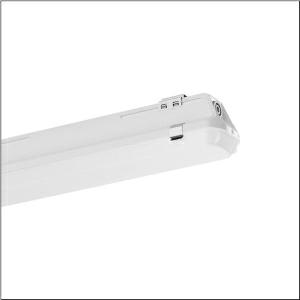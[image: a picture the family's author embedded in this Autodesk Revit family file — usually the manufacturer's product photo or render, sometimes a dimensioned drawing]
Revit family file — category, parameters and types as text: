
# Revit family: monsun_r__21_51fb107p420b_fb8a
name_source: partatom
category: Lighting Fixtures
units: mm (PartAtom-declared; Revit-internal decimal feet)

## family parameters
Cut with Voids When Loaded = No
Host = Face
Light Source = No
Part Type = Normal
Room Calculation Point = No
Round Connector Dimension = Use Diameter
Shared = No

## types (1)
- Monsun® 21 (1 x LED, 2580 lm, 17.5 W, 4000K)
    Apparent Load = 18 VA
    CIE Flux Codes = 47 77 93 94 100
    Color Rendering = 80
    Color Temperature = 4000K
    Default Elevation = 1800 mm
    Description = Monsun® 21, damp-proof luminaire, chain hanger, primary optical cover: enclosure, of PMMA, light emission: direct distribution, primary light characteristic: symmetric, installation type: suspended mounting, surface-mounted, horizontal mounting, vertical mounting, LED, rated luminous flux: 2.580lm, luminous efficacy: 147lm/W, light colour: 840, colour temperature: 4000K, control gear: ECG, with terminal, 3-pole, max. 2.5mm², mains connection: 220..240V, AC, 50/60Hz, rated input power: 18W, housing, of glass-fibre reinforced polyester, uncoated, bright grey, incl. chain hanger, length: 1.590mm, width: 90mm, height: 88mm, clip for enclosure, of stainless steel (V2A), ceiling mounting element, of stainless steel (V2A), chain hanger, of stainless steel (V2A), protection rating (complete): IP66, insulation class (complete): insulation class I (protective earthing), certification: CE, ENEC, VDE, UKCA, protection symbol: D, impact resistance: IK04, permissible operating ambient temperature: -25..+35°C, standard: EN 50419, EN 60598-2-1, corresponds to IFS (International Featured Standards) requirements for safety and quality in the food industry, for indoor or canopied outdoor use, no direct snow, no direct sun, no direct rain, contact your sales advisor before using the luminaires in applications with unclear chemical exposure, large temperature fluctuations or condensation-forming humidity, LABS conformity tested according to VDMA 24364:2018-05, packaging unit: 1 piece
    Height = 89 mm
    Lamp = 1 x LED
    Lamp Light Flux = 2580 lm
    Lamp Power = 17.5 W
    Lamp count = 1
    Length = 1590 mm
    Luminous efficacy = 147 lm/W
    Manufacturer = Siteco
    ModVariant = No
    Model = 51FB107P420B
    Mounting Place = Ceiling
    Mounting Type = Surface mounted
    Number of Poles = 1
    OnlyDefault = Yes
    Power Factor = 1
    Product Name = Monsun® 21
    Product group = damp-proof luminaire
    ProductGroupID = 301
    Protection Class = Protection class I
    Protection Degree = IP 66
    RLX_Detail_Level = 1
    RLX_Emergency_Light_Flux = 0 lm
    RLX_Emergency_Type = 0
    RLX_Emergency_Type_DB = No
    RlxData = <blob elided: 88245 chars, md5=88641d09>
    Socket = socket
    Standby Power = 0 W
    System Light Flux = 2580 lm
    System Power = 18 W
    Type Comments = Product without accessories
    Type Image = l_1006717.jpg
    URL = http://relux.com
    VarID = ---
    Voltage = 0 V
    Weight = 0.00 kg
    Width = 90 mm

## geometry (parser evidence)
native form markers: Blend x4, Sweep x12
no freeform markers — native parametric forms only
